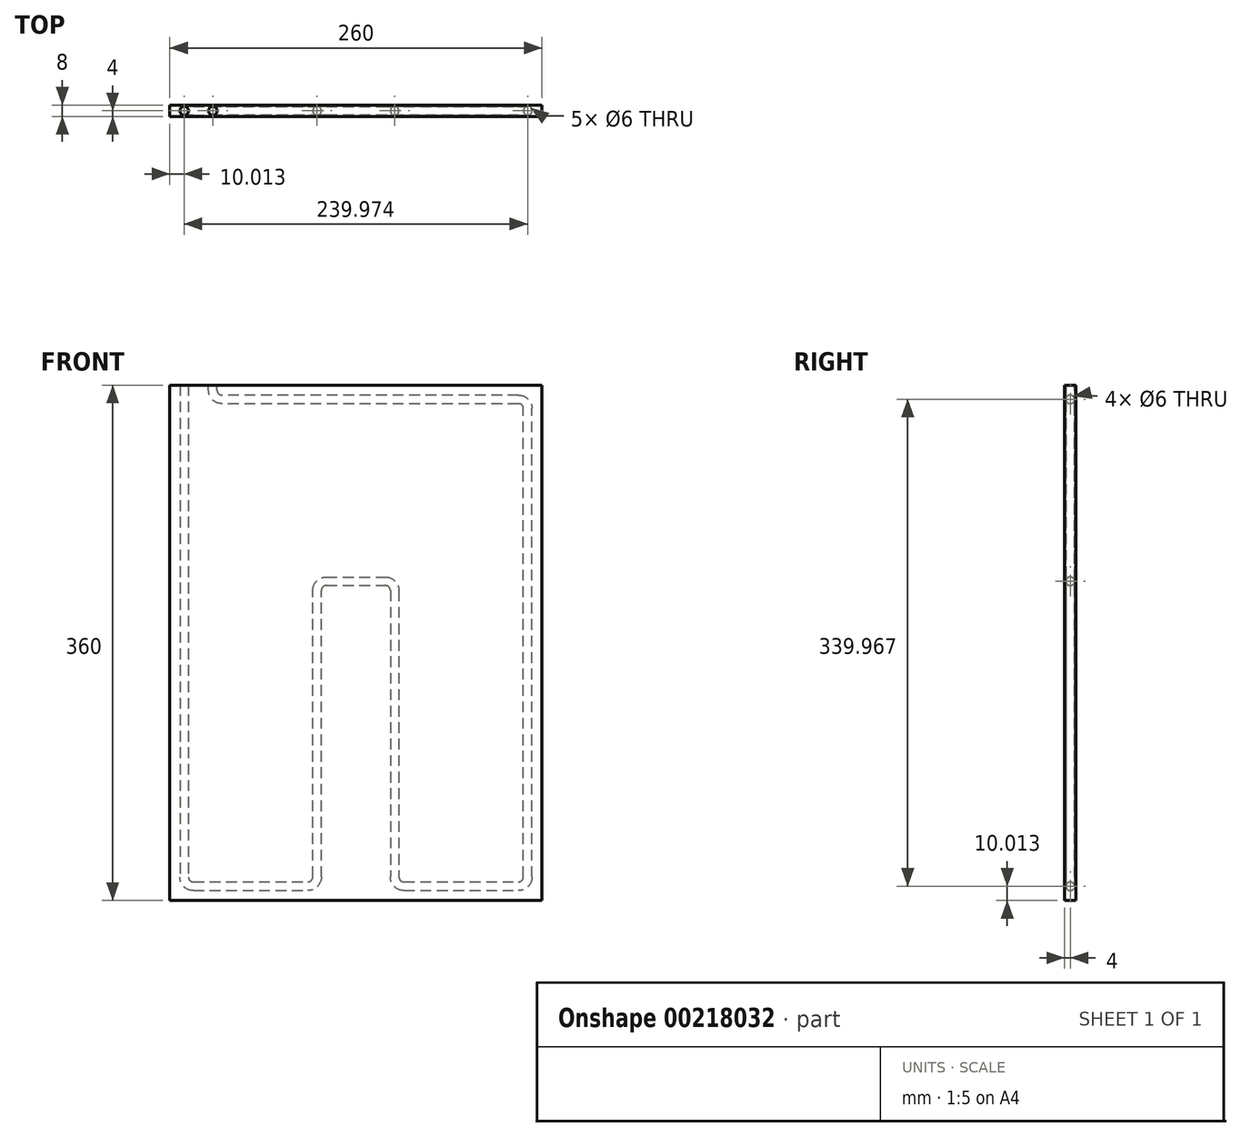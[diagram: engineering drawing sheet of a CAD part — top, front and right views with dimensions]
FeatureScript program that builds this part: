
annotation { "Feature Type Name" : "Feature", "Feature Type Description" : "" }
export const myFeature = defineFeature(function(context is Context, id is Id, definition is map)
    precondition{}
    {
        {
            var Q0;
            Q0=qCreatedBy(makeId("Front.planeOp"),FACE);
            var sketch = newSketch(context, id + "F0", { "sketchPlane" : qUnion([Q0])});
            skLineSegment(sketch, "E0.bottom", {"start": v(130, 180) * mm, "end": v(-130, 180) * mm});
            skLineSegment(sketch, "E0.top", {"start": v(130, -180) * mm, "end": v(-130, -180) * mm});
            skLineSegment(sketch, "E0.left", {"start": v(130, 180) * mm, "end": v(130, -180) * mm});
            skLineSegment(sketch, "E0.right", {"start": v(-130, 180) * mm, "end": v(-130, -180) * mm});
            skPoint(sketch, "E0.middle", {"position": v(0, 0) * mm});
            skSolve(sketch);
        }
        {
            var Q0;
            Q0=makeQuery(id+"F0.imprint","IMPRINT",FACE,{"disambiguationData":[TD([[makeQuery(id+"F0.imprint","IMPRINT",EDGE,{"derivedFrom":sQuery(id+"F0.wireOp",EDGE,"E0.bottom")}),1.0]])]});
            var sketch = newSketch(context, id + "F1", { "sketchPlane" : qUnion([Q0])});
            skLineSegment(sketch, "E1", {"start": v(-120, 189.9) * mm, "end": v(-120, -163.65) * mm});
            skLineSegment(sketch, "E2", {"start": v(113.65, 170) * mm, "end": v(-93.65, 170) * mm});
            skLineSegment(sketch, "E3", {"start": v(-100, 176.34) * mm, "end": v(-100, 189.9) * mm});
            skPoint(sketch, "E4.visualSharp", {"position": v(-120, -170) * mm});
            skArc(sketch, "E4.filletArc", {"start": v(-120, -163.65) * mm, "mid": v(-118.14, -168.14) * mm, "end": v(-113.65, -170) * mm});
            skPoint(sketch, "E5.visualSharp", {"position": v(-100, -170) * mm});
            skPoint(sketch, "E6.visualSharp", {"position": v(60, 170) * mm});
            skArc(sketch, "E6.filletArc", {"start": v(120, 163.64) * mm, "mid": v(118.14, 168.13) * mm, "end": v(113.65, 170) * mm});
            skPoint(sketch, "E7.visualSharp", {"position": v(-100, 170) * mm});
            skArc(sketch, "E7.filletArc", {"start": v(-100, 176.34) * mm, "mid": v(-98.14, 171.85) * mm, "end": v(-93.65, 170) * mm});
            skLineSegment(sketch, "E8", {"start": v(-27.15, -163.5) * mm, "end": v(-27.15, 36.5) * mm});
            skLineSegment(sketch, "E9", {"start": v(-20.65, 43) * mm, "end": v(20.5, 43) * mm});
            skPoint(sketch, "E10.visualSharp", {"position": v(-27.15, 43) * mm});
            skArc(sketch, "E10.filletArc", {"start": v(-20.65, 43) * mm, "mid": v(-25.25, 41.1) * mm, "end": v(-27.15, 36.5) * mm});
            skPoint(sketch, "E11.visualSharp", {"position": v(-27.15, -170) * mm});
            skArc(sketch, "E11.filletArc", {"start": v(-33.65, -170) * mm, "mid": v(-29.05, -168.1) * mm, "end": v(-27.15, -163.5) * mm});
            skLineSegment(sketch, "E12", {"start": v(27, 36.5) * mm, "end": v(27, -163.5) * mm});
            skLineSegment(sketch, "E13", {"start": v(33.5, -170) * mm, "end": v(113.5, -170) * mm});
            skLineSegment(sketch, "E14", {"start": v(120, -163.5) * mm, "end": v(120, 163.64) * mm});
            skPoint(sketch, "E15.visualSharp", {"position": v(27, -170) * mm});
            skArc(sketch, "E15.filletArc", {"start": v(27, -163.5) * mm, "mid": v(28.9, -168.1) * mm, "end": v(33.5, -170) * mm});
            skPoint(sketch, "E16.visualSharp", {"position": v(120, -170) * mm});
            skArc(sketch, "E16.filletArc", {"start": v(113.5, -170) * mm, "mid": v(118.1, -168.1) * mm, "end": v(120, -163.5) * mm});
            skPoint(sketch, "E17.visualSharp", {"position": v(27, 43) * mm});
            skArc(sketch, "E17.filletArc", {"start": v(27, 36.5) * mm, "mid": v(25.1, 41.1) * mm, "end": v(20.5, 43) * mm});
            skLineSegment(sketch, "E18", {"start": v(-113.65, -170) * mm, "end": v(-33.65, -170) * mm});
            skSolve(sketch);
        }
        {
            var Q0;
            Q0=makeQuery(id+"F0.imprint","IMPRINT",FACE,{"disambiguationData":[TD([[makeQuery(id+"F0.imprint","IMPRINT",EDGE,{"derivedFrom":sQuery(id+"F0.wireOp",EDGE,"E0.bottom")}),1.0]])]});
            extrude(context, id + "F2", {"entities" : qUnion([Q0]), "depth" : 8 * mm, "symmetric" : true});
        }
        {
            var Q0;
            Q0=sQuery(id+"F1.wireOp",VERTEX,"E3.end");
            var Q1;
            Q1=qCreatedBy(makeId("Top.planeOp"),FACE);
            cPlane(context, id + "F3", {"entities" : qUnion([Q0, Q1]), "cplaneType" : CPlaneType.PLANE_POINT, "offset" : 25.4 * mm, "width" : 152.4 * mm, "height" : 152.4 * mm});
        }
        {
            var Q0;
            Q0=qCreatedBy(id+"F3.planeOp",FACE);
            var sketch = newSketch(context, id + "F4", { "sketchPlane" : qUnion([Q0])});
            skCircle(sketch, "E19", {"center": v(-119.99, 0) * mm, "radius": 3 * mm});
            skCircle(sketch, "E20", {"center": v(-100, 0) * mm, "radius": 3 * mm});
            skSolve(sketch);
        }
        {
            var Q0;
            Q0=makeQuery(id+"F4.imprint","IMPRINT",FACE,{"disambiguationData":[TD([[makeQuery(id+"F4.imprint","IMPRINT",EDGE,{"derivedFrom":sQuery(id+"F4.wireOp",EDGE,"E19")}),1.0]])]});
            var Q1;
            Q1=sQuery(id+"F1.wireOp",EDGE,"E1");
            var Q2;
            Q2=sQuery(id+"F1.wireOp",EDGE,"E4.filletArc");
            var Q3;
            Q3=sQuery(id+"F1.wireOp",EDGE,"E18");
            var Q4;
            Q4=sQuery(id+"F1.wireOp",EDGE,"E11.filletArc");
            var Q5;
            Q5=sQuery(id+"F1.wireOp",EDGE,"E8");
            var Q6;
            Q6=sQuery(id+"F1.wireOp",EDGE,"E10.filletArc");
            var Q7;
            Q7=sQuery(id+"F1.wireOp",EDGE,"E9");
            var Q8;
            Q8=sQuery(id+"F1.wireOp",EDGE,"E17.filletArc");
            var Q9;
            Q9=sQuery(id+"F1.wireOp",EDGE,"E12");
            var Q10;
            Q10=sQuery(id+"F1.wireOp",EDGE,"E15.filletArc");
            var Q11;
            Q11=sQuery(id+"F1.wireOp",EDGE,"E13");
            var Q12;
            Q12=sQuery(id+"F1.wireOp",EDGE,"E16.filletArc");
            var Q13;
            Q13=sQuery(id+"F1.wireOp",EDGE,"E14");
            var Q14;
            Q14=sQuery(id+"F1.wireOp",EDGE,"E6.filletArc");
            var Q15;
            Q15=sQuery(id+"F1.wireOp",EDGE,"E2");
            var Q16;
            Q16=sQuery(id+"F1.wireOp",EDGE,"E7.filletArc");
            var Q17;
            Q17=sQuery(id+"F1.wireOp",EDGE,"E3");
            sweep(context, id + "F5", {"operationType" : NewBodyOperationType.REMOVE, "profiles" : qUnion([Q0]), "path" : qUnion([Q1, Q2, Q3, Q4, Q5, Q6, Q7, Q8, Q9, Q10, Q11, Q12, Q13, Q14, Q15, Q16, Q17])});
        }
    });
